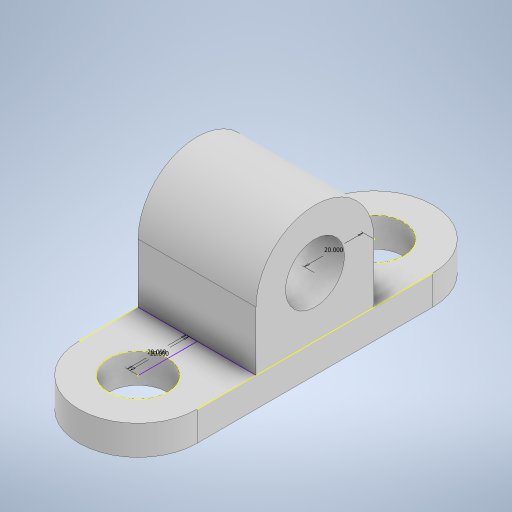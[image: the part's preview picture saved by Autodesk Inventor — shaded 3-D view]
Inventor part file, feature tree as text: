
AUTODESK INVENTOR PART (.ipt)
format: ipt  version: 2024 (Build 280153000, 153)  size: 277,504 bytes
history: native  units: in
note: dims shown in document units (in); Inventor stores cm internally (conversion verified against a paired STEP export)
features: sketch x11, extrude x2
ambient origin geometry x8: Origin, YZ Plane, XZ Plane, XY Plane, X Axis, Y Axis, Z Axis, Center Point
bodies: Solid1 (feature_tree)
feature tree (13):
  extrude  "Extrusion1"  Depth=40.0in
  sketch  "Sketch2"  dims[d2=80.0in d3=20.0in]
  sketch  "Sketch3"  dims[d4=20.0in]
  sketch  "Sketch4"  dims[d7=10.0in d8=0.0in]
  sketch  "Sketch5"  dims[d9=20.0in]
  sketch  "Sketch6"  dims[d10=20.0in]
  sketch  "Sketch7"  dims[d11=20.0in]
  sketch  "Sketch8"  dims[d12=20.0in]
  sketch  "Sketch9"  dims[d13=20.0in]
  sketch  "3D Sketch1"
  extrude  "Extrusion2"  Depth=20.0in
  sketch  "Sketch1"  dims[d0=80.0in d1=40.0in]
  sketch  "Sketch10"  dims[d14=40.0in d15=20.0in d16=20.0in d17=40.0in d18=0.0in d19=0.5in d20=0.0344in]
